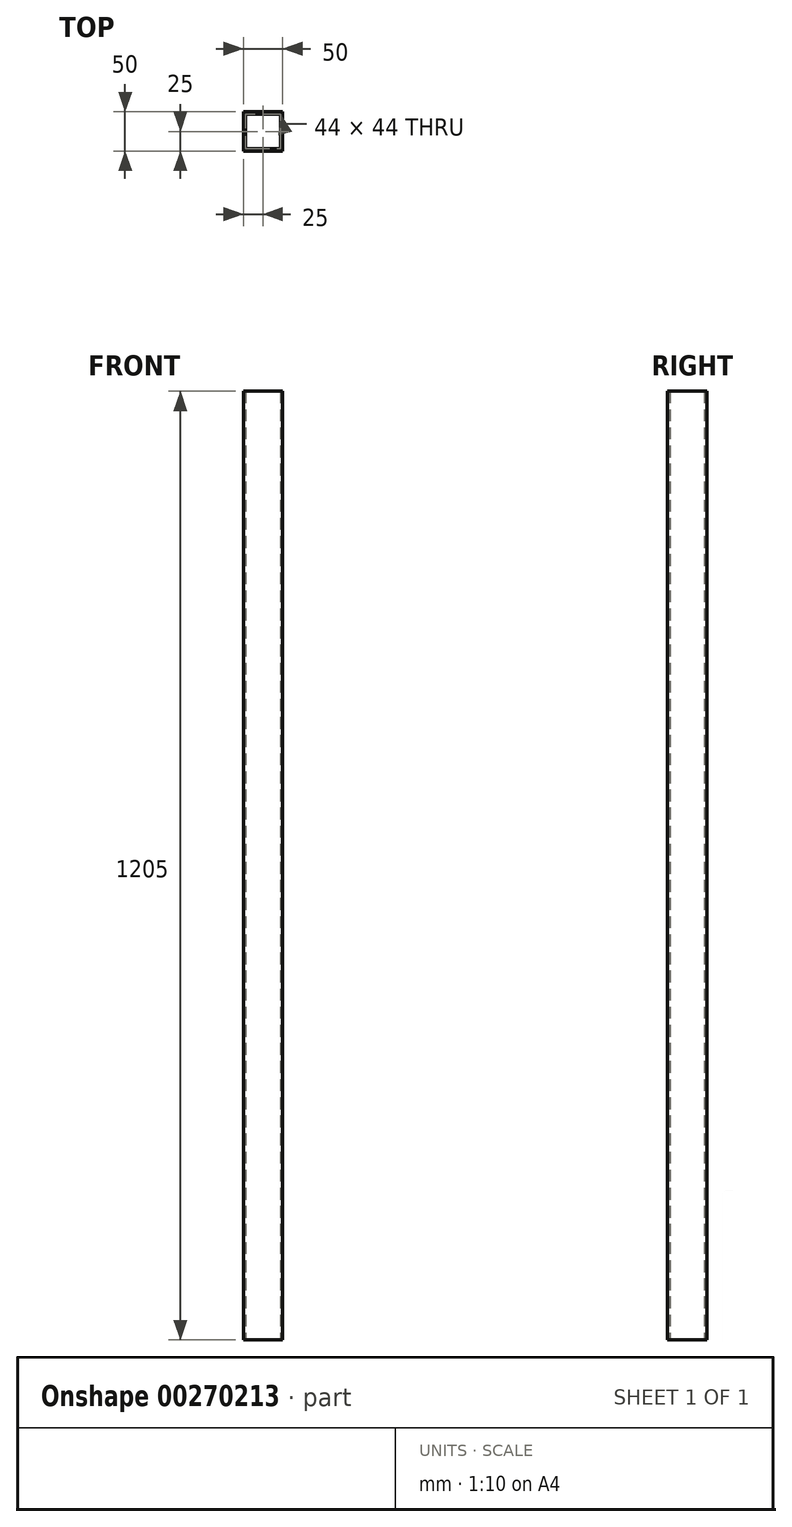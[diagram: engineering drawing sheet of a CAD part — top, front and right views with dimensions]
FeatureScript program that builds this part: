
annotation { "Feature Type Name" : "Feature", "Feature Type Description" : "" }
export const myFeature = defineFeature(function(context is Context, id is Id, definition is map)
    precondition{}
    {
        {
            var Q0;
            Q0=qCreatedBy(makeId("Top.planeOp"),FACE);
            var sketch = newSketch(context, id + "F0", { "sketchPlane" : qUnion([Q0])});
            skLineSegment(sketch, "E0.bottom", {"start": v(25, -25) * mm, "end": v(-25, -25) * mm});
            skLineSegment(sketch, "E0.top", {"start": v(25, 25) * mm, "end": v(-25, 25) * mm});
            skLineSegment(sketch, "E0.left", {"start": v(25, -25) * mm, "end": v(25, 25) * mm});
            skLineSegment(sketch, "E0.right", {"start": v(-25, -25) * mm, "end": v(-25, 25) * mm});
            skPoint(sketch, "E0.middle", {"position": v(0, 0) * mm});
            skLineSegment(sketch, "E1.bottom", {"start": v(22, -22) * mm, "end": v(-22, -22) * mm});
            skLineSegment(sketch, "E1.top", {"start": v(22, 22) * mm, "end": v(-22, 22) * mm});
            skLineSegment(sketch, "E1.left", {"start": v(22, -22) * mm, "end": v(22, 22) * mm});
            skLineSegment(sketch, "E1.right", {"start": v(-22, -22) * mm, "end": v(-22, 22) * mm});
            skSolve(sketch);
        }
        {
            var Q0;
            Q0=makeQuery(id+"F0.imprint","IMPRINT",FACE,{"disambiguationData":[TD([[makeQuery(id+"F0.imprint","IMPRINT",EDGE,{"derivedFrom":sQuery(id+"F0.wireOp",EDGE,"E0.bottom")}),-1.0]])]});
            extrude(context, id + "F1", {"entities" : qUnion([Q0]), "depth" : 1205 * mm});
        }
    });
